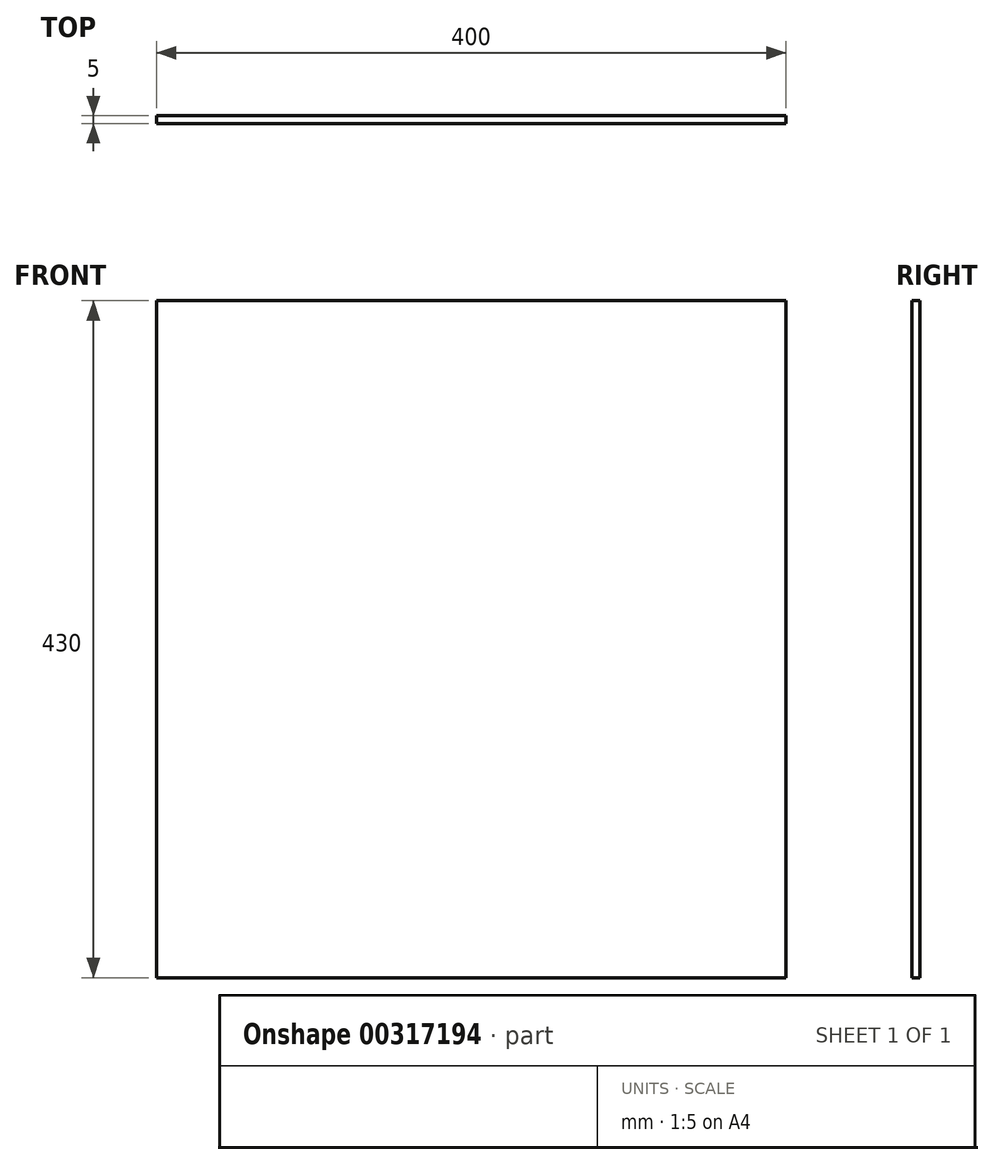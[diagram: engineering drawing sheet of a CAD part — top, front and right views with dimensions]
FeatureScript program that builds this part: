
annotation { "Feature Type Name" : "Feature", "Feature Type Description" : "" }
export const myFeature = defineFeature(function(context is Context, id is Id, definition is map)
    precondition{}
    {
        {
            var Q0;
            Q0=qCreatedBy(makeId("Front.planeOp"),FACE);
            var sketch = newSketch(context, id + "F0", { "sketchPlane" : qUnion([Q0])});
            skLineSegment(sketch, "E0.bottom", {"start": v(-200, 215) * mm, "end": v(200, 215) * mm});
            skLineSegment(sketch, "E0.top", {"start": v(-200, -215) * mm, "end": v(200, -215) * mm});
            skLineSegment(sketch, "E0.left", {"start": v(-200, 215) * mm, "end": v(-200, -215) * mm});
            skLineSegment(sketch, "E0.right", {"start": v(200, 215) * mm, "end": v(200, -215) * mm});
            skLineSegment(sketch, "E1", {"start": v(-200, 215) * mm, "end": v(200, -215) * mm, "construction": true});
            skSolve(sketch);
        }
        {
            var Q0;
            Q0 = qSketchRegion(id + "F0", true);
            extrude(context, id + "F1", {"entities" : qUnion([Q0]), "depth" : 5 * mm});
        }
    });
